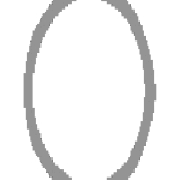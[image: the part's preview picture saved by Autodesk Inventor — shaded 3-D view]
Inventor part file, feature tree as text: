
AUTODESK INVENTOR PART (.ipt)
format: ipt  version: 2021 (Build 250183000, 183)  size: 112,128 bytes
history: native  units: in
note: dims shown in document units (in); Inventor stores cm internally (conversion verified against a paired STEP export)
features: other x4, sketch x3, plane x1
ambient origin geometry x8: Origin, YZ Plane, XZ Plane, XY Plane, X Axis, Y Axis, Z Axis, Center Point
bodies: Solid1 (feature_tree), Body (feature_tree)
feature tree (8):
  other  "Driven Length"
  other  "Frame Generator"
  other  "Start Plane"
  other  "End Plane"
  sketch  "Sketch"  dims[d2=5.831in d4=-0.0in d5=5.831in d6=0.12in d7=0.0in d10=90.0deg d9=5.831in]
  sketch  "Sketch4"  dims[d0=1.0in]
  plane  "Work Plane4"
  sketch  "Sketch5"  dims[d1=0.065in]
